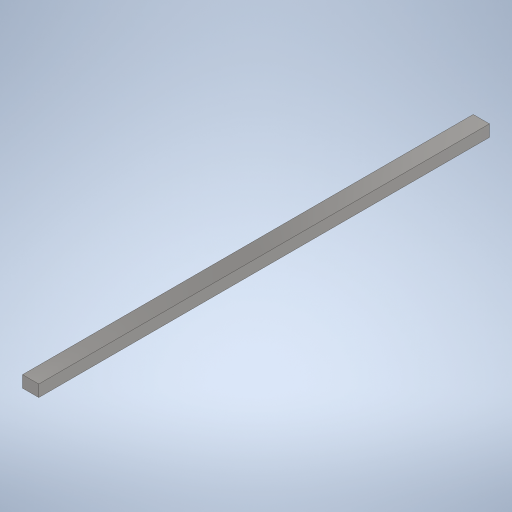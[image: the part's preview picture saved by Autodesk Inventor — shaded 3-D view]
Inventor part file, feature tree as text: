
AUTODESK INVENTOR PART (.ipt)
format: ipt  version: 2024 (Build 280153000, 153)  size: 234,496 bytes
history: native  units: in
note: dims shown in document units (in); Inventor stores cm internally (conversion verified against a paired STEP export)
features: extrude x1, sketch x1
ambient origin geometry x8: Origin, YZ Plane, XZ Plane, XY Plane, X Axis, Y Axis, Z Axis, Center Point
bodies: Solid1 (feature_tree)
feature tree (2):
  extrude  "Extrusion1"  Depth=0.2559in
  sketch  "Sketch1"  dims[d0=0.3543in d1=0.2559in d2=9.8425in d3=0.0in]
